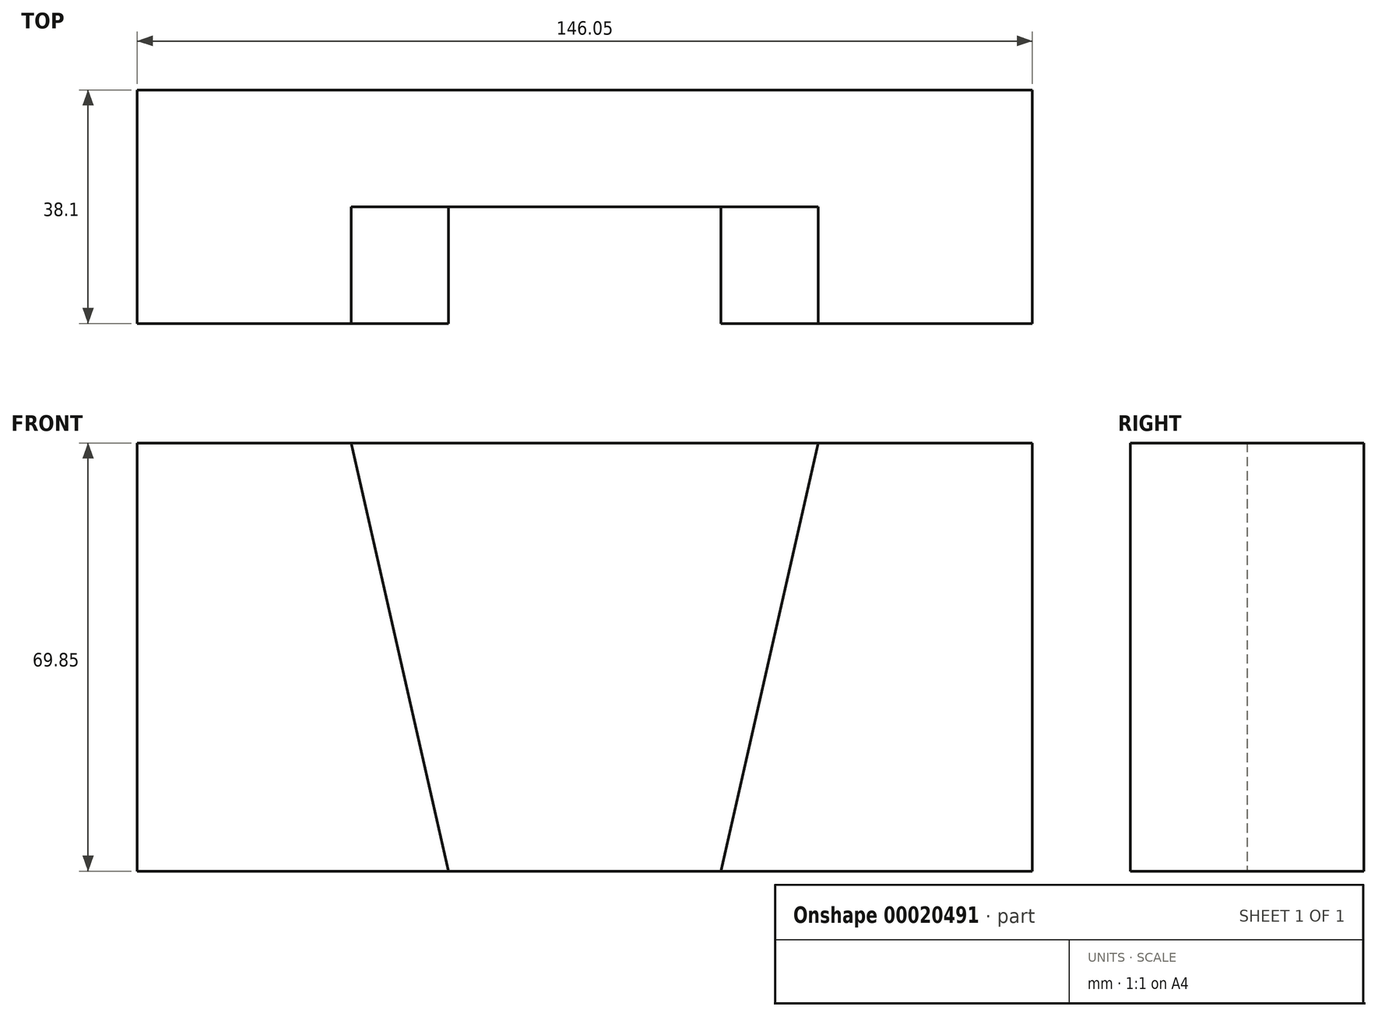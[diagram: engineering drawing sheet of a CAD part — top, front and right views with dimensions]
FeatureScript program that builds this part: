
annotation { "Feature Type Name" : "Feature", "Feature Type Description" : "" }
export const myFeature = defineFeature(function(context is Context, id is Id, definition is map)
    precondition{}
    {
        {
            var Q0;
            Q0=qCreatedBy(makeId("Front.planeOp"),FACE);
            var sketch = newSketch(context, id + "F0", { "sketchPlane" : qUnion([Q0])});
            skLineSegment(sketch, "E0", {"start": v(-83.65, 35.38) * mm, "end": v(-83.65, -34.47) * mm});
            skLineSegment(sketch, "E1", {"start": v(-83.65, -34.47) * mm, "end": v(-32.85, -34.47) * mm});
            skLineSegment(sketch, "E2", {"start": v(-10.62, -34.47) * mm, "end": v(-10.62, 35.38) * mm});
            skLineSegment(sketch, "E3", {"start": v(-83.65, 35.38) * mm, "end": v(-48.72, 35.38) * mm});
            skPoint(sketch, "E4.orphan", {"position": v(-10.62, 38.04) * mm});
            skLineSegment(sketch, "E5", {"start": v(-32.85, -34.47) * mm, "end": v(-10.62, -34.47) * mm});
            skLineSegment(sketch, "E6", {"start": v(-48.72, 35.38) * mm, "end": v(-10.62, 35.38) * mm});
            skLineSegment(sketch, "E7", {"start": v(-48.72, 35.38) * mm, "end": v(-32.85, -34.47) * mm});
            skSolve(sketch);
        }
        {
            var Q0;
            Q0=makeQuery(id+"F0.imprint","IMPRINT",FACE,{"disambiguationData":[TD([[makeQuery(id+"F0.imprint","IMPRINT",EDGE,{"derivedFrom":sQuery(id+"F0.wireOp",EDGE,"E0")}),1.0]])]});
            extrude(context, id + "F1", {"entities" : qUnion([Q0]), "depth" : 38.1 * mm});
        }
        {
            var Q0;
            Q0=makeQuery(id+"F0.imprint","IMPRINT",FACE,{"disambiguationData":[TD([[makeQuery(id+"F0.imprint","IMPRINT",EDGE,{"derivedFrom":sQuery(id+"F0.wireOp",EDGE,"E2")}),1.0]])]});
            extrude(context, id + "F2", {"entities" : qUnion([Q0]), "operationType" : NewBodyOperationType.ADD, "depth" : 19.05 * mm});
        }
        {
            var Q0;
            Q0=makeQuery(id+"F1.opExtrude","SWEPT_BODY",BODY,{"disambiguationData":[OSD([sQuery(id+"F0.wireOp",EDGE,"E0"),sQuery(id+"F0.wireOp",EDGE,"E1"),sQuery(id+"F0.wireOp",EDGE,"E3"),sQuery(id+"F0.wireOp",EDGE,"E7")])]});
            var Q1;
            Q1=makeQuery(id+"F2.opExtrude","SWEPT_FACE",FACE,{"disambiguationData":[OSD([sQuery(id+"F0.wireOp",EDGE,"E2")])]});
            mirror(context, id + "F3", {"operationType" : NewBodyOperationType.ADD, "entities" : qUnion([Q0]), "mirrorPlane" : qUnion([Q1])});
        }
    });
